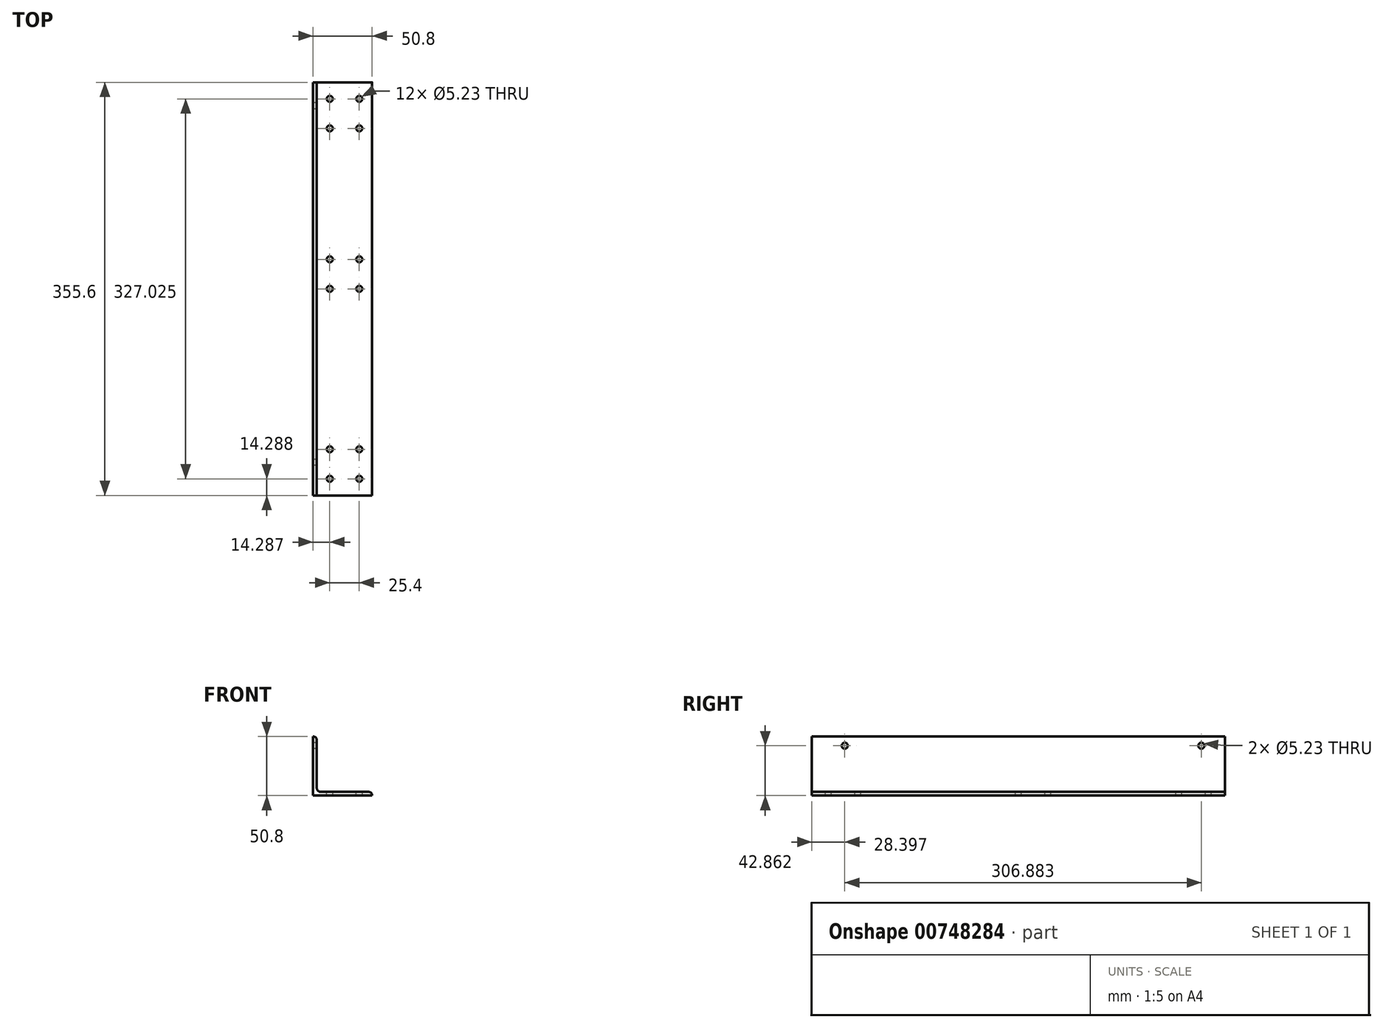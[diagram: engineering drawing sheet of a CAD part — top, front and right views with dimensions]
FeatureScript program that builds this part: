
annotation { "Feature Type Name" : "Feature", "Feature Type Description" : "" }
export const myFeature = defineFeature(function(context is Context, id is Id, definition is map)
    precondition{}
    {
        {
            var Q0;
            Q0=qCreatedBy(makeId("Front.planeOp"),FACE);
            var sketch = newSketch(context, id + "F0", { "sketchPlane" : qUnion([Q0])});
            skLineSegment(sketch, "E0", {"start": v(0, 0) * mm, "end": v(-50.8, 0) * mm});
            skLineSegment(sketch, "E1", {"start": v(-50.8, 0) * mm, "end": v(-50.8, 50.8) * mm});
            skLineSegment(sketch, "E2", {"start": v(-50.8, 50.8) * mm, "end": v(-50.8, 50.8) * mm});
            skLineSegment(sketch, "E3", {"start": v(-47.63, 47.63) * mm, "end": v(-47.63, 6.35) * mm});
            skLineSegment(sketch, "E4", {"start": v(-44.45, 3.18) * mm, "end": v(-3.18, 3.18) * mm});
            skLineSegment(sketch, "E5", {"start": v(0, 0) * mm, "end": v(0, 0) * mm});
            skPoint(sketch, "E6.visualSharp", {"position": v(-47.63, 3.18) * mm});
            skArc(sketch, "E6.filletArc", {"start": v(-47.63, 6.35) * mm, "mid": v(-46.7, 4.1) * mm, "end": v(-44.45, 3.18) * mm});
            skPoint(sketch, "E7.visualSharp", {"position": v(-47.63, 50.8) * mm});
            skArc(sketch, "E7.filletArc", {"start": v(-47.63, 47.63) * mm, "mid": v(-48.55, 49.87) * mm, "end": v(-50.8, 50.8) * mm});
            skPoint(sketch, "E8.visualSharp", {"position": v(0, 3.18) * mm});
            skArc(sketch, "E8.filletArc", {"start": v(0, 0) * mm, "mid": v(-0.93, 2.25) * mm, "end": v(-3.18, 3.18) * mm});
            skSolve(sketch);
        }
        {
            var Q0;
            Q0=qSketchRegion(id+"F0",true);
            extrude(context, id + "F1", {"entities" : qUnion([Q0]), "depth" : 355.6 * mm, "offsetDistance" : 25.4 * mm});
        }
        {
            var Q0;
            Q0=makeQuery(id+"F1.opExtrude","SWEPT_FACE",FACE,{"disambiguationData":[OSD([sQuery(id+"F0.wireOp",EDGE,"E4")])]});
            var sketch = newSketch(context, id + "F2", { "sketchPlane" : qUnion([Q0])});
            skLineSegment(sketch, "E9", {"start": v(-23.81, -355.6) * mm, "end": v(-23.81, 0) * mm, "construction": true});
            skLineSegment(sketch, "E10", {"start": v(-3.18, -341.31) * mm, "end": v(-44.45, -341.31) * mm, "construction": true});
            skCircle(sketch, "E11", {"center": v(-36.51, -341.31) * mm, "radius": 2.62 * mm});
            skLineSegment(sketch, "E12", {"start": v(-44.45, -14.29) * mm, "end": v(-3.18, -14.29) * mm, "construction": true});
            skCircle(sketch, "E13", {"center": v(-36.51, -14.29) * mm, "radius": 2.62 * mm});
            skLineSegment(sketch, "E14", {"start": v(-3.18, -177.8) * mm, "end": v(-44.45, -177.8) * mm, "construction": true});
            skLineSegment(sketch, "E15.0", {"start": v(-3.17, -257.18) * mm, "end": v(-19.05, -257.18) * mm, "construction": true});
            skCircle(sketch, "E16", {"center": v(-36.51, -177.8) * mm, "radius": 2.62 * mm});
            skLineSegment(sketch, "E17", {"start": v(-36.51, 0) * mm, "end": v(-36.51, -355.6) * mm, "construction": true});
            skLineSegment(sketch, "E18", {"start": v(-3.18, -152.4) * mm, "end": v(-44.45, -152.4) * mm, "construction": true});
            skLineSegment(sketch, "E19", {"start": v(-11.11, 0) * mm, "end": v(-11.11, -355.6) * mm, "construction": true});
            skCircle(sketch, "E20", {"center": v(-11.11, -152.4) * mm, "radius": 2.62 * mm});
            skCircle(sketch, "E21", {"center": v(-11.11, -177.8) * mm, "radius": 2.62 * mm});
            skCircle(sketch, "E22", {"center": v(-36.51, -152.4) * mm, "radius": 2.62 * mm});
            skCircle(sketch, "E23", {"center": v(-11.11, -14.29) * mm, "radius": 2.62 * mm});
            skCircle(sketch, "E24", {"center": v(-11.11, -341.31) * mm, "radius": 2.62 * mm});
            skLineSegment(sketch, "E25", {"start": v(-44.45, -39.69) * mm, "end": v(-3.17, -39.69) * mm, "construction": true});
            skCircle(sketch, "E26", {"center": v(-36.51, -39.69) * mm, "radius": 2.62 * mm});
            skCircle(sketch, "E27", {"center": v(-11.11, -39.69) * mm, "radius": 2.62 * mm});
            skLineSegment(sketch, "E28", {"start": v(-44.45, -315.91) * mm, "end": v(-3.17, -315.91) * mm, "construction": true});
            skCircle(sketch, "E29", {"center": v(-36.51, -315.91) * mm, "radius": 2.62 * mm});
            skCircle(sketch, "E30", {"center": v(-11.11, -315.91) * mm, "radius": 2.62 * mm});
            skSolve(sketch);
        }
        {
            var Q0;
            Q0=qSketchRegion(id+"F2",true);
            extrude(context, id + "F3", {"entities" : qUnion([Q0]), "operationType" : NewBodyOperationType.REMOVE, "endBound" : BoundingType.THROUGH_ALL, "oppositeDirection" : true, "depth" : 25.4 * mm, "offsetDistance" : 25.4 * mm});
        }
        {
            var Q0;
            Q0=makeQuery(id+"F1.opExtrude","SWEPT_FACE",FACE,{"disambiguationData":[OSD([sQuery(id+"F0.wireOp",EDGE,"E1")])]});
            var sketch = newSketch(context, id + "F4", { "sketchPlane" : qUnion([Q0])});
            skLineSegment(sketch, "E31", {"start": v(0, 42.86) * mm, "end": v(355.6, 42.86) * mm, "construction": true});
            skCircle(sketch, "E32", {"center": v(20.32, 42.86) * mm, "radius": 2.62 * mm});
            skCircle(sketch, "E33", {"center": v(327.2, 42.86) * mm, "radius": 2.62 * mm});
            skSolve(sketch);
        }
        {
            var Q0;
            Q0 = qSketchRegion(id + "F4", true);
            extrude(context, id + "F5", {"entities" : qUnion([Q0]), "operationType" : NewBodyOperationType.REMOVE, "endBound" : BoundingType.THROUGH_ALL, "oppositeDirection" : true, "depth" : 25.4 * mm, "offsetDistance" : 25.4 * mm});
        }
    });
